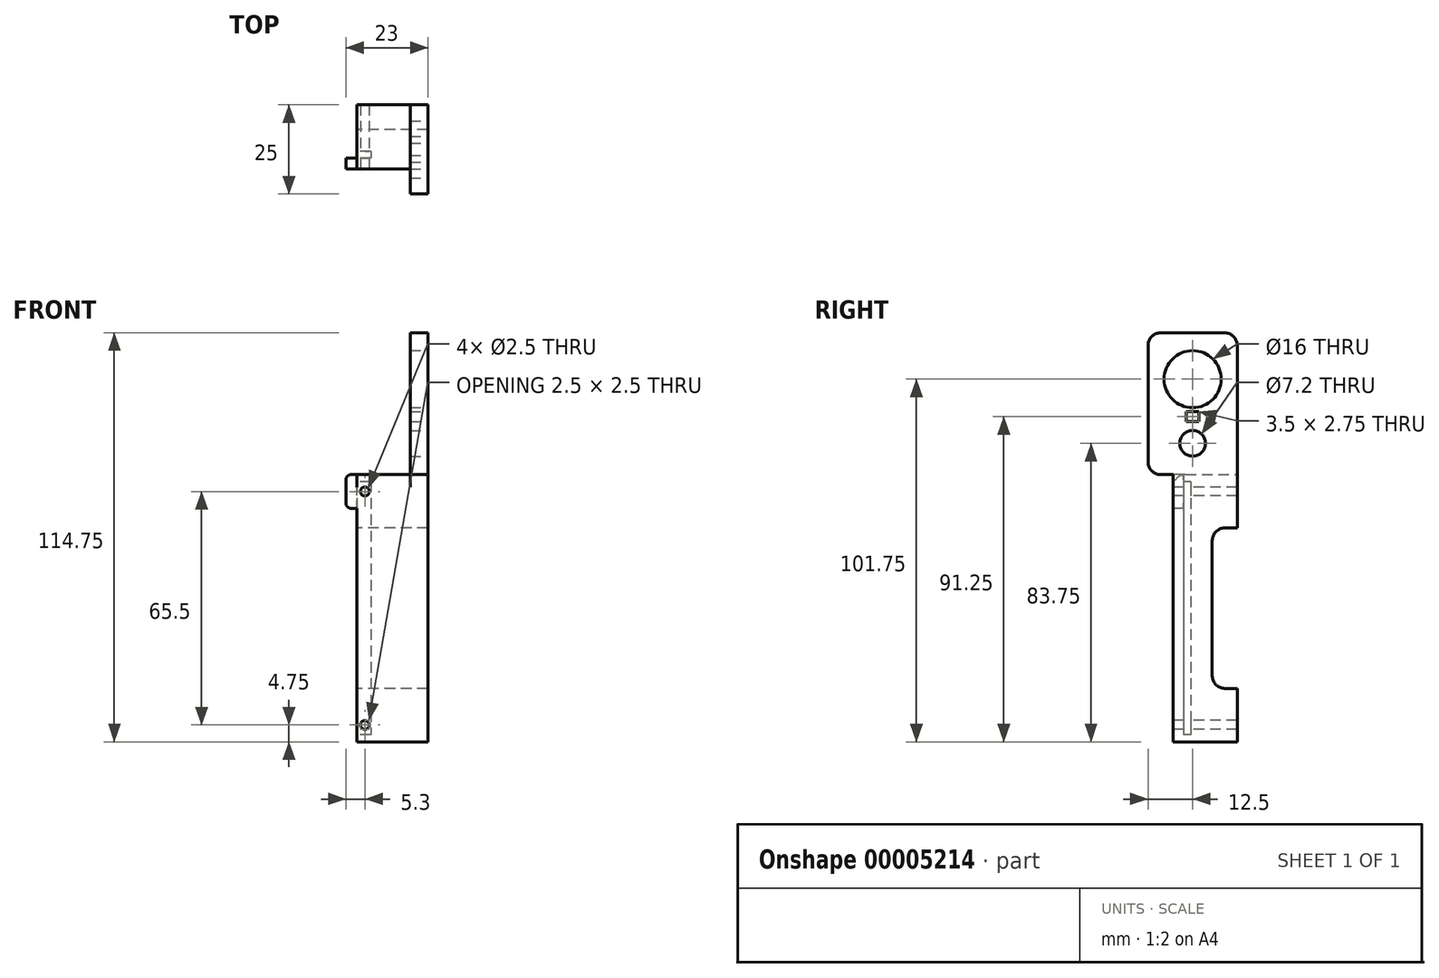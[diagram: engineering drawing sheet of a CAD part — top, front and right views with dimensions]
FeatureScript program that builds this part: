
annotation { "Feature Type Name" : "Feature", "Feature Type Description" : "" }
export const myFeature = defineFeature(function(context is Context, id is Id, definition is map)
    precondition{}
    {
        {
            var Q0;
            Q0=qCreatedBy(makeId("Front.planeOp"),FACE);
            var sketch = newSketch(context, id + "F0", { "sketchPlane" : qUnion([Q0])});
            skLineSegment(sketch, "E0.bottom", {"start": v(0, 0) * mm, "end": v(20, 0) * mm});
            skLineSegment(sketch, "E0.top", {"start": v(0, 75) * mm, "end": v(20, 75) * mm});
            skLineSegment(sketch, "E0.left", {"start": v(0, 0) * mm, "end": v(0, 75) * mm});
            skLineSegment(sketch, "E0.right", {"start": v(20, 0) * mm, "end": v(20, 75) * mm});
            skSolve(sketch);
        }
        {
            var Q0;
            Q0 = qSketchRegion(id + "F0", true);
            extrude(context, id + "F1", {"entities" : qUnion([Q0]), "depth" : 18 * mm, "offsetDistance" : 25 * mm});
        }
        {
            var Q0;
            Q0=makeQuery(id+"F1.opExtrude","SWEPT_FACE",FACE,{"disambiguationData":[OSD([sQuery(id+"F0.wireOp",EDGE,"E0.left")])]});
            var sketch = newSketch(context, id + "F2", { "sketchPlane" : qUnion([Q0])});
            skLineSegment(sketch, "E1", {"start": v(18, 37.5) * mm, "end": v(0, 37.5) * mm, "construction": true});
            skLineSegment(sketch, "E2.bottom", {"start": v(13, 73) * mm, "end": v(15, 73) * mm});
            skLineSegment(sketch, "E2.top", {"start": v(13, 2) * mm, "end": v(15, 2) * mm});
            skLineSegment(sketch, "E2.left", {"start": v(13, 73) * mm, "end": v(13, 2) * mm});
            skLineSegment(sketch, "E2.right", {"start": v(15, 73) * mm, "end": v(15, 2) * mm});
            skSolve(sketch);
        }
        {
            var Q0;
            Q0 = qSketchRegion(id + "F2", true);
            extrude(context, id + "F3", {"entities" : qUnion([Q0]), "operationType" : NewBodyOperationType.REMOVE, "oppositeDirection" : true, "depth" : 4 * mm, "offsetDistance" : 25 * mm});
        }
        {
            var Q0;
            Q0=makeQuery(id+"F1.opExtrude","CAP_FACE",FACE,{"disambiguationData":[OSD([sQuery(id+"F0.wireOp",EDGE,"E0.bottom"),sQuery(id+"F0.wireOp",EDGE,"E0.top"),sQuery(id+"F0.wireOp",EDGE,"E0.left"),sQuery(id+"F0.wireOp",EDGE,"E0.right")])],"isStart":false});
            var sketch = newSketch(context, id + "F4", { "sketchPlane" : qUnion([Q0])});
            skLineSegment(sketch, "E3.0", {"start": v(4, 73) * mm, "end": v(4, 2) * mm, "construction": true});
            skLineSegment(sketch, "E4", {"start": v(0, 37.5) * mm, "end": v(20, 37.5) * mm, "construction": true});
            skCircle(sketch, "E5", {"center": v(2.3, 70.25) * mm, "radius": 1.25 * mm});
            skCircle(sketch, "E6.MirrorC", {"center": v(2.3, 4.75) * mm, "radius": 1.25 * mm});
            skSolve(sketch);
        }
        {
            var Q0;
            Q0 = qSketchRegion(id + "F4", true);
            extrude(context, id + "F5", {"entities" : qUnion([Q0]), "operationType" : NewBodyOperationType.REMOVE, "endBound" : BoundingType.THROUGH_ALL, "oppositeDirection" : true, "depth" : 20 * mm, "offsetDistance" : 25 * mm});
        }
        {
            var Q0;
            Q0=makeQuery(id+"F1.opExtrude","SWEPT_FACE",FACE,{"disambiguationData":[OSD([sQuery(id+"F0.wireOp",EDGE,"E0.right")])]});
            var sketch = newSketch(context, id + "F6", { "sketchPlane" : qUnion([Q0])});
            skLineSegment(sketch, "E7.bottom", {"start": v(0, 75) * mm, "end": v(-25, 75) * mm});
            skLineSegment(sketch, "E7.top", {"start": v(0, 114.75) * mm, "end": v(-25, 114.75) * mm});
            skLineSegment(sketch, "E7.left", {"start": v(0, 75) * mm, "end": v(0, 114.75) * mm});
            skLineSegment(sketch, "E7.right", {"start": v(-25, 75) * mm, "end": v(-25, 114.75) * mm});
            skLineSegment(sketch, "E8", {"start": v(-12.5, 114.75) * mm, "end": v(-12.5, 75) * mm, "construction": true});
            skCircle(sketch, "E9", {"center": v(-12.5, 83.75) * mm, "radius": 8.75 * mm, "construction": true});
            skCircle(sketch, "E10", {"center": v(-12.5, 101.75) * mm, "radius": 8 * mm});
            skCircle(sketch, "E11", {"center": v(-12.5, 83.75) * mm, "radius": 3.6 * mm});
            skLineSegment(sketch, "E12.bottom", {"start": v(-10.75, 89.88) * mm, "end": v(-14.25, 89.88) * mm});
            skLineSegment(sketch, "E12.top", {"start": v(-10.75, 92.62) * mm, "end": v(-14.25, 92.62) * mm});
            skLineSegment(sketch, "E12.left", {"start": v(-10.75, 89.88) * mm, "end": v(-10.75, 92.62) * mm});
            skLineSegment(sketch, "E12.right", {"start": v(-14.25, 89.88) * mm, "end": v(-14.25, 92.62) * mm});
            skPoint(sketch, "E12.middle", {"position": v(-12.5, 91.25) * mm});
            skSolve(sketch);
        }
        {
            var Q0;
            Q0 = qSketchRegion(id + "F6", true);
            extrude(context, id + "F7", {"entities" : qUnion([Q0]), "operationType" : NewBodyOperationType.ADD, "oppositeDirection" : true, "depth" : 5 * mm, "offsetDistance" : 25 * mm});
        }
        {
            var Q0;
            Q0=makeQuery(id+"F1.opExtrude","SWEPT_FACE",FACE,{"disambiguationData":[OSD([sQuery(id+"F0.wireOp",EDGE,"E0.left")])]});
            var sketch = newSketch(context, id + "F8", { "sketchPlane" : qUnion([Q0])});
            skLineSegment(sketch, "E13.bottom", {"start": v(0, 60) * mm, "end": v(7, 60) * mm});
            skLineSegment(sketch, "E13.top", {"start": v(0, 15) * mm, "end": v(7, 15) * mm});
            skLineSegment(sketch, "E13.left", {"start": v(0, 60) * mm, "end": v(0, 15) * mm});
            skLineSegment(sketch, "E13.right", {"start": v(7, 60) * mm, "end": v(7, 15) * mm});
            skLineSegment(sketch, "E14", {"start": v(18, 37.5) * mm, "end": v(31.23, 37.5) * mm, "construction": true});
            skSolve(sketch);
        }
        {
            var Q0;
            Q0 = qSketchRegion(id + "F8", true);
            extrude(context, id + "F9", {"entities" : qUnion([Q0]), "operationType" : NewBodyOperationType.REMOVE, "endBound" : BoundingType.THROUGH_ALL, "oppositeDirection" : true, "depth" : 25 * mm, "offsetDistance" : 25 * mm});
        }
        {
            var Q0;
            Q0=makeQuery(id+"F7.opExtrude","SWEPT_EDGE",EDGE,{"disambiguationData":[OSD([sQuery(id+"F6.wireOp",EDGE,"E7.bottom"),sQuery(id+"F6.wireOp",EDGE,"E7.right")])]});
            var Q1;
            {var subQ0=sQuery(id+"F0.wireOp",EDGE,"E0.top");Q1=makeQuery(id+"F7.boolean.opBoolean","SPLIT",EDGE,{"disambiguationData":[topologyDisambiguationEdgeConnected([makeQuery(id+"F7.opExtrude","SWEPT_FACE",FACE,{"disambiguationData":[OSD([sQuery(id+"F6.wireOp",EDGE,"E7.bottom")])]})])],"derivedFrom":makeQuery(id+"F1.opExtrude","CAP_EDGE",EDGE,{"disambiguationData":[OSD([subQ0])],"isStart":false})});}
            var Q2;
            Q2=makeQuery(id+"F7.opExtrude","SWEPT_EDGE",EDGE,{"disambiguationData":[OSD([sQuery(id+"F6.wireOp",EDGE,"E7.top"),sQuery(id+"F6.wireOp",EDGE,"E7.right")])]});
            var Q3;
            Q3=makeQuery(id+"F7.opExtrude","SWEPT_EDGE",EDGE,{"disambiguationData":[OSD([sQuery(id+"F6.wireOp",EDGE,"E7.top"),sQuery(id+"F6.wireOp",EDGE,"E7.left")])]});
            var Q4;
            Q4=makeQuery(id+"F9.boolean.opBoolean","COPY",EDGE,{"derivedFrom":makeQuery(id+"F9.opExtrude","SWEPT_EDGE",EDGE,{"disambiguationData":[OSD([sQuery(id+"F0.wireOp",EDGE,"E0.left"),sQuery(id+"F8.wireOp",EDGE,"E13.bottom"),sQuery(id+"F8.wireOp",EDGE,"E13.left")])]})});
            var Q5;
            Q5=makeQuery(id+"F9.boolean.opBoolean","COPY",EDGE,{"derivedFrom":makeQuery(id+"F9.opExtrude","SWEPT_EDGE",EDGE,{"disambiguationData":[OSD([sQuery(id+"F8.wireOp",EDGE,"E13.bottom"),sQuery(id+"F8.wireOp",EDGE,"E13.right")])]})});
            var Q6;
            Q6=makeQuery(id+"F9.boolean.opBoolean","COPY",EDGE,{"derivedFrom":makeQuery(id+"F9.opExtrude","SWEPT_EDGE",EDGE,{"disambiguationData":[OSD([sQuery(id+"F8.wireOp",EDGE,"E13.top"),sQuery(id+"F8.wireOp",EDGE,"E13.right")])]})});
            var Q7;
            Q7=makeQuery(id+"F9.boolean.opBoolean","COPY",EDGE,{"derivedFrom":makeQuery(id+"F9.opExtrude","SWEPT_EDGE",EDGE,{"disambiguationData":[OSD([sQuery(id+"F0.wireOp",EDGE,"E0.left"),sQuery(id+"F8.wireOp",EDGE,"E13.top"),sQuery(id+"F8.wireOp",EDGE,"E13.left")])]})});
            fillet(context, id + "F10", {"entities" : qUnion([Q0, Q1, Q2, Q3, Q4, Q5, Q6, Q7]), "tangentPropagation" : true, "radius" : 3.5 * mm, "defaultsChanged" : false, "vertexSettings" : [], "allowEdgeOverflow" : false});
        }
        {
            var Q0;
            Q0=makeQuery(id+"F1.opExtrude","CAP_FACE",FACE,{"disambiguationData":[OSD([sQuery(id+"F0.wireOp",EDGE,"E0.bottom"),sQuery(id+"F0.wireOp",EDGE,"E0.top"),sQuery(id+"F0.wireOp",EDGE,"E0.left"),sQuery(id+"F0.wireOp",EDGE,"E0.right")])],"isStart":false});
            var sketch = newSketch(context, id + "F11", { "sketchPlane" : qUnion([Q0])});
            skLineSegment(sketch, "E15.bottom", {"start": v(0, 75) * mm, "end": v(-3, 75) * mm});
            skLineSegment(sketch, "E15.top", {"start": v(0, 65.5) * mm, "end": v(-3, 65.5) * mm});
            skLineSegment(sketch, "E15.left", {"start": v(0, 75) * mm, "end": v(0, 65.5) * mm});
            skLineSegment(sketch, "E15.right", {"start": v(-3, 75) * mm, "end": v(-3, 65.5) * mm});
            skLineSegment(sketch, "E16", {"start": v(2.3, 70.25) * mm, "end": v(0, 70.25) * mm, "construction": true});
            skSolve(sketch);
        }
        {
            var Q0;
            Q0 = qSketchRegion(id + "F11", true);
            var Q1;
            Q1=makeQuery(id+"F3.boolean.opBoolean","COPY",FACE,{"derivedFrom":makeQuery(id+"F3.opExtrude","SWEPT_FACE",FACE,{"disambiguationData":[OSD([sQuery(id+"F2.wireOp",EDGE,"E2.right")])]})});
            extrude(context, id + "F12", {"entities" : qUnion([Q0]), "operationType" : NewBodyOperationType.ADD, "endBound" : BoundingType.UP_TO_SURFACE, "oppositeDirection" : true, "depth" : 25 * mm, "endBoundEntityFace" : qUnion([Q1]), "offsetDistance" : 25 * mm});
        }
        {
            var Q0;
            Q0=makeQuery(id+"F12.opExtrude","SWEPT_EDGE",EDGE,{"disambiguationData":[OSD([sQuery(id+"F11.wireOp",EDGE,"E15.top"),sQuery(id+"F11.wireOp",EDGE,"E15.right")])]});
            var Q1;
            Q1=makeQuery(id+"F12.opExtrude","SWEPT_EDGE",EDGE,{"disambiguationData":[OSD([sQuery(id+"F11.wireOp",EDGE,"E15.bottom"),sQuery(id+"F11.wireOp",EDGE,"E15.right")])]});
            var Q2;
            Q2=makeQuery(id+"F12.opExtrude","SWEPT_EDGE",EDGE,{"disambiguationData":[OSD([sQuery(id+"F0.wireOp",EDGE,"E0.left"),sQuery(id+"F11.wireOp",EDGE,"E15.top"),sQuery(id+"F11.wireOp",EDGE,"E15.left")])]});
            fillet(context, id + "F13", {"entities" : qUnion([Q0, Q1, Q2]), "tangentPropagation" : true, "radius" : 1.5 * mm, "defaultsChanged" : false, "vertexSettings" : [], "allowEdgeOverflow" : false});
        }
    });
